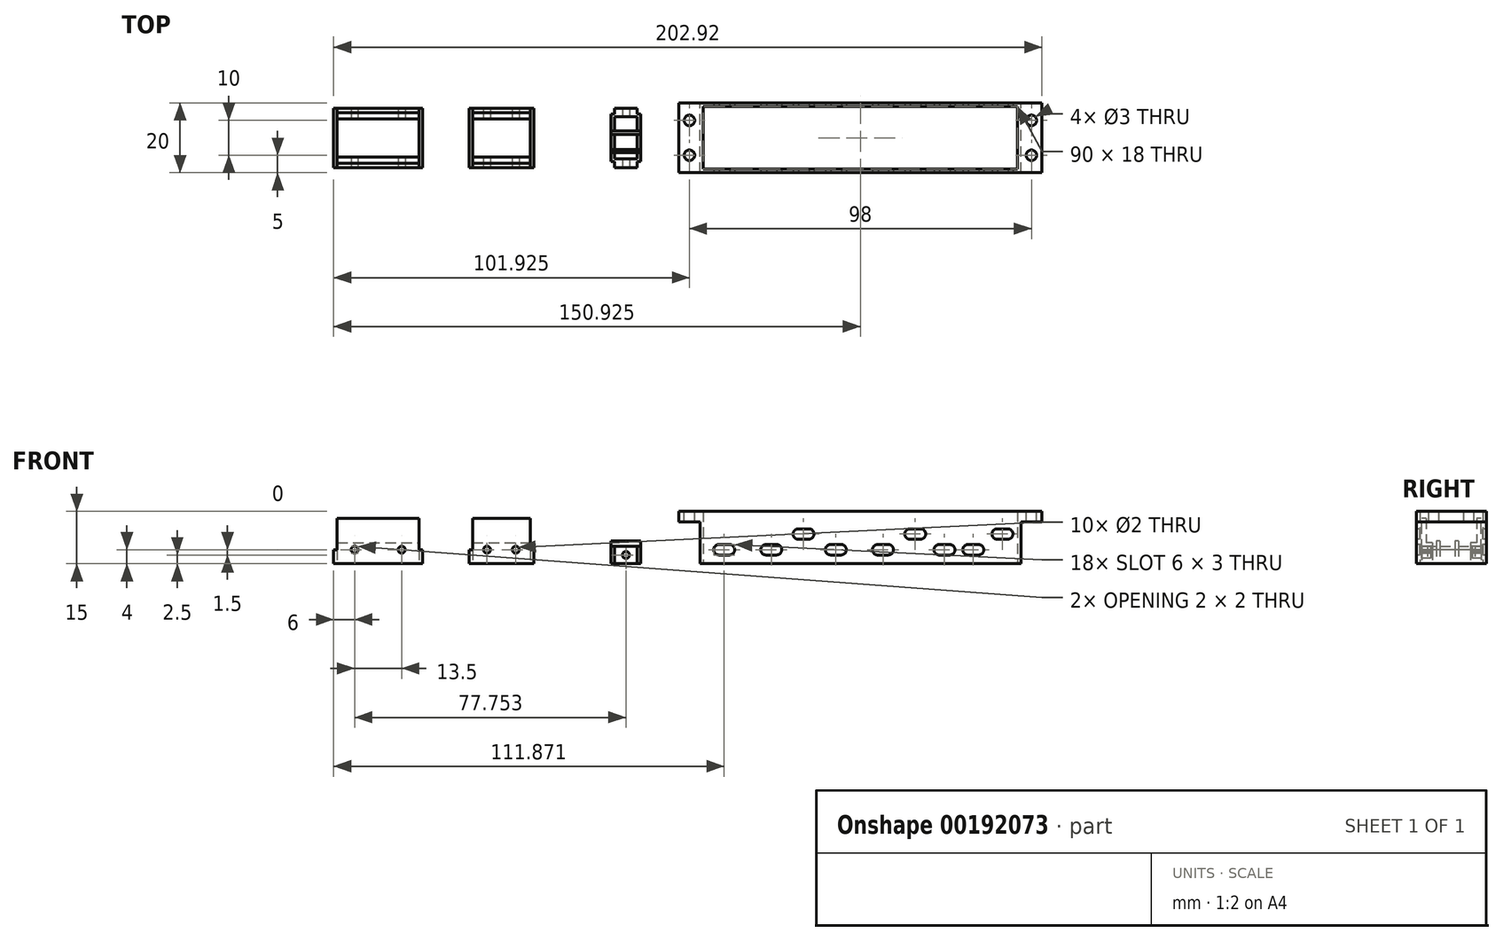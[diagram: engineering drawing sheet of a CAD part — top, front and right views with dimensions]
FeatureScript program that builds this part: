
annotation { "Feature Type Name" : "Feature", "Feature Type Description" : "" }
export const myFeature = defineFeature(function(context is Context, id is Id, definition is map)
    precondition{}
    {
        {
            var Q0;
            Q0=qCreatedBy(makeId("Top.planeOp"),FACE);
            var sketch = newSketch(context, id + "F0", { "sketchPlane" : qUnion([Q0])});
            skLineSegment(sketch, "E0.bottom", {"start": v(11.75, -7.25) * mm, "end": v(-11.75, -7.25) * mm});
            skLineSegment(sketch, "E0.top", {"start": v(11.75, 7.25) * mm, "end": v(-11.75, 7.25) * mm});
            skLineSegment(sketch, "E0.left", {"start": v(11.75, -7.25) * mm, "end": v(11.75, 7.25) * mm});
            skLineSegment(sketch, "E0.right", {"start": v(-11.75, -7.25) * mm, "end": v(-11.75, 7.25) * mm});
            skPoint(sketch, "E0.middle", {"position": v(0, 0) * mm});
            skLineSegment(sketch, "E1.bottom", {"start": v(12.75, -8.5) * mm, "end": v(-12.75, -8.5) * mm});
            skLineSegment(sketch, "E1.top", {"start": v(12.75, 8.5) * mm, "end": v(-12.75, 8.5) * mm});
            skLineSegment(sketch, "E1.left", {"start": v(12.75, -8.5) * mm, "end": v(12.75, 8.5) * mm});
            skLineSegment(sketch, "E1.right", {"start": v(-12.75, -8.5) * mm, "end": v(-12.75, 8.5) * mm});
            skLineSegment(sketch, "E2.bottom", {"start": v(26.05, -8.5) * mm, "end": v(44.55, -8.5) * mm});
            skLineSegment(sketch, "E2.top", {"start": v(26.05, 8.5) * mm, "end": v(44.55, 8.5) * mm});
            skLineSegment(sketch, "E2.left", {"start": v(26.05, -8.5) * mm, "end": v(26.05, 8.5) * mm});
            skLineSegment(sketch, "E2.right", {"start": v(44.55, -8.5) * mm, "end": v(44.55, 8.5) * mm});
            skPoint(sketch, "E2.middle", {"position": v(35.3, 0) * mm});
            skLineSegment(sketch, "E3.bottom", {"start": v(43.55, -7.25) * mm, "end": v(27.05, -7.25) * mm});
            skLineSegment(sketch, "E3.top", {"start": v(43.55, 7.25) * mm, "end": v(27.05, 7.25) * mm});
            skLineSegment(sketch, "E3.left", {"start": v(43.55, -7.25) * mm, "end": v(43.55, 7.25) * mm});
            skLineSegment(sketch, "E3.right", {"start": v(27.05, -7.25) * mm, "end": v(27.05, 7.25) * mm});
            skSolve(sketch);
        }
        {
            var Q0;
            Q0 = qSketchRegion(id + "F0", true);
            extrude(context, id + "F1", {"entities" : qUnion([Q0]), "depth" : 13 * mm});
        }
        {
            var Q0;
            Q0=qCreatedBy(makeId("Top.planeOp"),FACE);
            var sketch = newSketch(context, id + "F2", { "sketchPlane" : qUnion([Q0])});
            skLineSegment(sketch, "E4.bottom", {"start": v(-11.75, 7.25) * mm, "end": v(11.75, 7.25) * mm});
            skLineSegment(sketch, "E4.top", {"start": v(-11.75, 5.45) * mm, "end": v(11.75, 5.45) * mm});
            skLineSegment(sketch, "E4.left", {"start": v(-11.75, 7.25) * mm, "end": v(-11.75, 5.45) * mm});
            skLineSegment(sketch, "E4.right", {"start": v(11.75, 7.25) * mm, "end": v(11.75, 5.45) * mm});
            skLineSegment(sketch, "E5.bottom", {"start": v(-11.75, -5.45) * mm, "end": v(11.75, -5.45) * mm});
            skLineSegment(sketch, "E5.top", {"start": v(-11.75, -7.25) * mm, "end": v(11.75, -7.25) * mm});
            skLineSegment(sketch, "E5.left", {"start": v(-11.75, -5.45) * mm, "end": v(-11.75, -7.25) * mm});
            skLineSegment(sketch, "E5.right", {"start": v(11.75, -5.45) * mm, "end": v(11.75, -7.25) * mm});
            skLineSegment(sketch, "E6.bottom", {"start": v(27.05, 7.25) * mm, "end": v(43.55, 7.25) * mm});
            skLineSegment(sketch, "E6.top", {"start": v(27.05, 5.45) * mm, "end": v(43.55, 5.45) * mm});
            skLineSegment(sketch, "E6.left", {"start": v(27.05, 7.25) * mm, "end": v(27.05, 5.45) * mm});
            skLineSegment(sketch, "E6.right", {"start": v(43.55, 7.25) * mm, "end": v(43.55, 5.45) * mm});
            skLineSegment(sketch, "E7.bottom", {"start": v(27.05, -5.45) * mm, "end": v(43.55, -5.45) * mm});
            skLineSegment(sketch, "E7.top", {"start": v(27.05, -7.25) * mm, "end": v(43.55, -7.25) * mm});
            skLineSegment(sketch, "E7.left", {"start": v(27.05, -5.45) * mm, "end": v(27.05, -7.25) * mm});
            skLineSegment(sketch, "E7.right", {"start": v(43.55, -5.45) * mm, "end": v(43.55, -7.25) * mm});
            skSolve(sketch);
        }
        {
            var Q0;
            Q0 = qSketchRegion(id + "F2", true);
            extrude(context, id + "F3", {"entities" : qUnion([Q0]), "operationType" : NewBodyOperationType.ADD, "depth" : 6 * mm});
        }
        {
            var Q0;
            Q0=makeQuery(id+"F1.opExtrude","CAP_FACE",FACE,{"disambiguationData":[OSD([sQuery(id+"F0.wireOp",EDGE,"E0.bottom"),sQuery(id+"F0.wireOp",EDGE,"E0.top"),sQuery(id+"F0.wireOp",EDGE,"E0.left"),sQuery(id+"F0.wireOp",EDGE,"E0.right"),sQuery(id+"F0.wireOp",EDGE,"E1.bottom"),sQuery(id+"F0.wireOp",EDGE,"E1.top"),sQuery(id+"F0.wireOp",EDGE,"E1.left"),sQuery(id+"F0.wireOp",EDGE,"E1.right")])],"isStart":false});
            var sketch = newSketch(context, id + "F4", { "sketchPlane" : qUnion([Q0])});
            skLineSegment(sketch, "E8.bottom", {"start": v(-12.75, 8.5) * mm, "end": v(-11.75, 8.5) * mm});
            skLineSegment(sketch, "E8.top", {"start": v(-12.75, -8.5) * mm, "end": v(-11.75, -8.5) * mm});
            skLineSegment(sketch, "E8.left", {"start": v(-12.75, 8.5) * mm, "end": v(-12.75, -8.5) * mm});
            skLineSegment(sketch, "E8.right", {"start": v(-11.75, 8.5) * mm, "end": v(-11.75, -8.5) * mm});
            skLineSegment(sketch, "E9.bottom", {"start": v(12.75, 8.5) * mm, "end": v(11.75, 8.5) * mm});
            skLineSegment(sketch, "E9.top", {"start": v(12.75, -8.5) * mm, "end": v(11.75, -8.5) * mm});
            skLineSegment(sketch, "E9.left", {"start": v(12.75, 8.5) * mm, "end": v(12.75, -8.5) * mm});
            skLineSegment(sketch, "E9.right", {"start": v(11.75, 8.5) * mm, "end": v(11.75, -8.5) * mm});
            skLineSegment(sketch, "E10.bottom", {"start": v(26.05, 8.5) * mm, "end": v(27.05, 8.5) * mm});
            skLineSegment(sketch, "E10.top", {"start": v(26.05, -8.5) * mm, "end": v(27.05, -8.5) * mm});
            skLineSegment(sketch, "E10.left", {"start": v(26.05, 8.5) * mm, "end": v(26.05, -8.5) * mm});
            skLineSegment(sketch, "E10.right", {"start": v(27.05, 8.5) * mm, "end": v(27.05, -8.5) * mm});
            skLineSegment(sketch, "E11.bottom", {"start": v(43.55, 8.5) * mm, "end": v(44.55, 8.5) * mm});
            skLineSegment(sketch, "E11.top", {"start": v(43.55, -8.5) * mm, "end": v(44.55, -8.5) * mm});
            skLineSegment(sketch, "E11.left", {"start": v(43.55, 8.5) * mm, "end": v(43.55, -8.5) * mm});
            skLineSegment(sketch, "E11.right", {"start": v(44.55, 8.5) * mm, "end": v(44.55, -8.5) * mm});
            skSolve(sketch);
        }
        {
            var Q0;
            Q0 = qSketchRegion(id + "F4", true);
            extrude(context, id + "F5", {"entities" : qUnion([Q0]), "operationType" : NewBodyOperationType.REMOVE, "oppositeDirection" : true, "depth" : 9 * mm});
        }
        {
            var Q0;
            Q0=qCreatedBy(makeId("Top.planeOp"),FACE);
            var sketch = newSketch(context, id + "F6", { "sketchPlane" : qUnion([Q0])});
            skLineSegment(sketch, "E12.left", {"start": v(67.75, -8.5) * mm, "end": v(67.75, 8.5) * mm});
            skLineSegment(sketch, "E12.right", {"start": v(66.75, -6.8) * mm, "end": v(66.75, 6.8) * mm});
            skPoint(sketch, "E12.middle", {"position": v(67.25, 0) * mm});
            skLineSegment(sketch, "E13.left", {"start": v(74.25, -8.5) * mm, "end": v(74.25, 8.5) * mm});
            skLineSegment(sketch, "E13.right", {"start": v(75.25, -6.8) * mm, "end": v(75.25, 6.8) * mm});
            skPoint(sketch, "E13.middle", {"position": v(74.75, 0) * mm});
            skLineSegment(sketch, "E14.bottom", {"start": v(67.75, 8.5) * mm, "end": v(74.25, 8.5) * mm});
            skLineSegment(sketch, "E14.top", {"start": v(67.75, 6) * mm, "end": v(74.25, 6) * mm});
            skLineSegment(sketch, "E14.left", {"start": v(67.75, 8.5) * mm, "end": v(67.75, 6) * mm});
            skLineSegment(sketch, "E14.right", {"start": v(74.25, 8.5) * mm, "end": v(74.25, 6) * mm});
            skLineSegment(sketch, "E15.bottom", {"start": v(67.75, -8.5) * mm, "end": v(74.25, -8.5) * mm});
            skLineSegment(sketch, "E15.top", {"start": v(67.75, -6) * mm, "end": v(74.25, -6) * mm});
            skLineSegment(sketch, "E15.left", {"start": v(67.75, -8.5) * mm, "end": v(67.75, -6) * mm});
            skLineSegment(sketch, "E15.right", {"start": v(74.25, -8.5) * mm, "end": v(74.25, -6) * mm});
            skLineSegment(sketch, "E16", {"start": v(66.75, 6.8) * mm, "end": v(67.75, 6.8) * mm});
            skLineSegment(sketch, "E17", {"start": v(74.25, 6.8) * mm, "end": v(75.25, 6.8) * mm});
            skLineSegment(sketch, "E18", {"start": v(74.25, -6.8) * mm, "end": v(75.25, -6.8) * mm});
            skLineSegment(sketch, "E19", {"start": v(66.75, -6.8) * mm, "end": v(67.75, -6.8) * mm});
            skSolve(sketch);
        }
        {
            var Q0;
            Q0 = qSketchRegion(id + "F6", true);
            extrude(context, id + "F7", {"entities" : qUnion([Q0]), "depth" : 5 * mm});
        }
        {
            var Q0;
            Q0=makeQuery(id+"F1.opExtrude","SWEPT_FACE",FACE,{"disambiguationData":[OSD([sQuery(id+"F0.wireOp",EDGE,"E1.bottom")])]});
            var sketch = newSketch(context, id + "F8", { "sketchPlane" : qUnion([Q0])});
            skCircle(sketch, "E20", {"center": v(-6.75, 4) * mm, "radius": 1 * mm});
            skCircle(sketch, "E21", {"center": v(6.75, 4) * mm, "radius": 1 * mm});
            skCircle(sketch, "E22", {"center": v(31.18, 4) * mm, "radius": 1 * mm});
            skCircle(sketch, "E23", {"center": v(39.43, 4) * mm, "radius": 1 * mm});
            skCircle(sketch, "E24", {"center": v(71, 2.5) * mm, "radius": 1 * mm});
            skSolve(sketch);
        }
        {
            var Q0;
            Q0 = qSketchRegion(id + "F8", true);
            extrude(context, id + "F9", {"entities" : qUnion([Q0]), "operationType" : NewBodyOperationType.REMOVE, "oppositeDirection" : true, "depth" : 25 * mm});
        }
        {
            var Q0;
            Q0=qCreatedBy(makeId("Top.planeOp"),FACE);
            var sketch = newSketch(context, id + "F10", { "sketchPlane" : qUnion([Q0])});
            skLineSegment(sketch, "E25.bottom", {"start": v(66.75, 2) * mm, "end": v(75.25, 2) * mm});
            skLineSegment(sketch, "E25.top", {"start": v(66.75, 1) * mm, "end": v(75.25, 1) * mm});
            skLineSegment(sketch, "E25.left", {"start": v(66.75, 2) * mm, "end": v(66.75, 1) * mm});
            skLineSegment(sketch, "E25.right", {"start": v(75.25, 2) * mm, "end": v(75.25, 1) * mm});
            skLineSegment(sketch, "E26.bottom", {"start": v(66.75, -3.3) * mm, "end": v(75.25, -3.3) * mm});
            skLineSegment(sketch, "E26.top", {"start": v(66.75, -4.3) * mm, "end": v(75.25, -4.3) * mm});
            skLineSegment(sketch, "E26.left", {"start": v(66.75, -3.3) * mm, "end": v(66.75, -4.3) * mm});
            skLineSegment(sketch, "E26.right", {"start": v(75.25, -3.3) * mm, "end": v(75.25, -4.3) * mm});
            skSolve(sketch);
        }
        {
            var Q0;
            Q0 = qSketchRegion(id + "F10", true);
            extrude(context, id + "F11", {"entities" : qUnion([Q0]), "operationType" : NewBodyOperationType.ADD, "depth" : 6.5 * mm});
        }
        {
            var Q0;
            Q0=qCreatedBy(makeId("Top.planeOp"),FACE);
            var sketch = newSketch(context, id + "F12", { "sketchPlane" : qUnion([Q0])});
            skLineSegment(sketch, "E27.bottom", {"start": v(183.17, -9) * mm, "end": v(93.17, -9) * mm});
            skLineSegment(sketch, "E27.top", {"start": v(183.17, 9) * mm, "end": v(93.17, 9) * mm});
            skLineSegment(sketch, "E27.left", {"start": v(183.17, -9) * mm, "end": v(183.17, 9) * mm});
            skLineSegment(sketch, "E27.right", {"start": v(93.17, -9) * mm, "end": v(93.17, 9) * mm});
            skPoint(sketch, "E27.middle", {"position": v(138.17, 0) * mm});
            skLineSegment(sketch, "E28.bottom", {"start": v(184.17, -10) * mm, "end": v(92.17, -10) * mm});
            skLineSegment(sketch, "E28.top", {"start": v(184.17, 10) * mm, "end": v(92.17, 10) * mm});
            skLineSegment(sketch, "E28.left", {"start": v(184.17, -10) * mm, "end": v(184.17, 10) * mm});
            skLineSegment(sketch, "E28.right", {"start": v(92.17, -10) * mm, "end": v(92.17, 10) * mm});
            skSolve(sketch);
        }
        {
            var Q0;
            Q0 = qSketchRegion(id + "F12", true);
            extrude(context, id + "F13", {"entities" : qUnion([Q0]), "depth" : 15 * mm});
        }
        {
            var Q0;
            Q0=makeQuery(id+"F13.opExtrude","CAP_FACE",FACE,{"disambiguationData":[OSD([sQuery(id+"F12.wireOp",EDGE,"E27.bottom"),sQuery(id+"F12.wireOp",EDGE,"E27.top"),sQuery(id+"F12.wireOp",EDGE,"E27.left"),sQuery(id+"F12.wireOp",EDGE,"E27.right"),sQuery(id+"F12.wireOp",EDGE,"E28.bottom"),sQuery(id+"F12.wireOp",EDGE,"E28.top"),sQuery(id+"F12.wireOp",EDGE,"E28.left"),sQuery(id+"F12.wireOp",EDGE,"E28.right")])],"isStart":false});
            var sketch = newSketch(context, id + "F14", { "sketchPlane" : qUnion([Q0])});
            skLineSegment(sketch, "E29.bottom", {"start": v(92.17, 10) * mm, "end": v(86.17, 10) * mm});
            skLineSegment(sketch, "E29.top", {"start": v(92.17, -10) * mm, "end": v(86.17, -10) * mm});
            skLineSegment(sketch, "E29.left", {"start": v(92.17, 10) * mm, "end": v(92.17, -10) * mm});
            skLineSegment(sketch, "E29.right", {"start": v(86.17, 10) * mm, "end": v(86.17, -10) * mm});
            skLineSegment(sketch, "E30.bottom", {"start": v(184.17, 10) * mm, "end": v(190.17, 10) * mm});
            skLineSegment(sketch, "E30.top", {"start": v(184.17, -10) * mm, "end": v(190.17, -10) * mm});
            skLineSegment(sketch, "E30.left", {"start": v(184.17, 10) * mm, "end": v(184.17, -10) * mm});
            skLineSegment(sketch, "E30.right", {"start": v(190.17, 10) * mm, "end": v(190.17, -10) * mm});
            skCircle(sketch, "E31", {"center": v(89.17, 5) * mm, "radius": 1.5 * mm});
            skCircle(sketch, "E32", {"center": v(89.17, -5) * mm, "radius": 1.5 * mm});
            skCircle(sketch, "E33", {"center": v(187.17, 5) * mm, "radius": 1.5 * mm});
            skCircle(sketch, "E34", {"center": v(187.17, -5) * mm, "radius": 1.5 * mm});
            skSolve(sketch);
        }
        {
            var Q0;
            Q0 = qSketchRegion(id + "F14", true);
            extrude(context, id + "F15", {"entities" : qUnion([Q0]), "operationType" : NewBodyOperationType.ADD, "oppositeDirection" : true, "depth" : 3 * mm});
        }
        {
            var Q0;
            Q0=makeQuery(id+"F15.boolean.opBoolean","MERGE",FACE,{"derivedFrom":[makeQuery(id+"F13.opExtrude","SWEPT_FACE",FACE,{"disambiguationData":[OSD([sQuery(id+"F12.wireOp",EDGE,"E28.bottom")])]}),makeQuery(id+"F15.opExtrude","SWEPT_FACE",FACE,{"disambiguationData":[OSD([sQuery(id+"F14.wireOp",EDGE,"E29.top")])]}),makeQuery(id+"F15.opExtrude","SWEPT_FACE",FACE,{"disambiguationData":[OSD([sQuery(id+"F14.wireOp",EDGE,"E30.top")])]})]});
            var sketch = newSketch(context, id + "F16", { "sketchPlane" : qUnion([Q0])});
            skLineSegment(sketch, "E35.bottom", {"start": v(100.73, 2.5) * mm, "end": v(97.73, 2.5) * mm});
            skLineSegment(sketch, "E35.top", {"start": v(100.62, 5.5) * mm, "end": v(97.62, 5.5) * mm});
            skPoint(sketch, "E35.middle", {"position": v(99.17, 4) * mm});
            skArc(sketch, "E36", {"start": v(97.62, 5.5) * mm, "mid": v(96.12, 3.94) * mm, "end": v(97.73, 2.5) * mm});
            skArc(sketch, "E37", {"start": v(100.62, 5.5) * mm, "mid": v(102.12, 4.05) * mm, "end": v(100.73, 2.5) * mm});
            skLineSegment(sketch, "E38.bottom", {"start": v(114.23, 2.5) * mm, "end": v(111.23, 2.5) * mm});
            skLineSegment(sketch, "E38.top", {"start": v(114.12, 5.5) * mm, "end": v(111.12, 5.5) * mm});
            skPoint(sketch, "E38.middle", {"position": v(112.67, 4) * mm});
            skArc(sketch, "E39", {"start": v(111.12, 5.5) * mm, "mid": v(109.62, 3.94) * mm, "end": v(111.23, 2.5) * mm});
            skArc(sketch, "E40", {"start": v(114.12, 5.5) * mm, "mid": v(115.62, 4.05) * mm, "end": v(114.23, 2.5) * mm});
            skLineSegment(sketch, "E41.bottom", {"start": v(132.73, 2.5) * mm, "end": v(129.73, 2.5) * mm});
            skLineSegment(sketch, "E41.top", {"start": v(132.62, 5.5) * mm, "end": v(129.62, 5.5) * mm});
            skPoint(sketch, "E41.middle", {"position": v(131.17, 4) * mm});
            skArc(sketch, "E42", {"start": v(129.62, 5.5) * mm, "mid": v(128.12, 3.94) * mm, "end": v(129.73, 2.5) * mm});
            skArc(sketch, "E43", {"start": v(132.62, 5.5) * mm, "mid": v(134.12, 4.05) * mm, "end": v(132.73, 2.5) * mm});
            skLineSegment(sketch, "E44.bottom", {"start": v(146.23, 2.5) * mm, "end": v(143.23, 2.5) * mm});
            skLineSegment(sketch, "E44.top", {"start": v(146.12, 5.5) * mm, "end": v(143.12, 5.5) * mm});
            skPoint(sketch, "E44.middle", {"position": v(144.67, 4) * mm});
            skArc(sketch, "E45", {"start": v(143.12, 5.5) * mm, "mid": v(141.62, 3.94) * mm, "end": v(143.23, 2.5) * mm});
            skArc(sketch, "E46", {"start": v(146.12, 5.5) * mm, "mid": v(147.62, 4.05) * mm, "end": v(146.23, 2.5) * mm});
            skLineSegment(sketch, "E47.bottom", {"start": v(163.85, 2.5) * mm, "end": v(160.85, 2.5) * mm});
            skLineSegment(sketch, "E47.top", {"start": v(163.75, 5.5) * mm, "end": v(160.75, 5.5) * mm});
            skPoint(sketch, "E47.middle", {"position": v(162.3, 4) * mm});
            skArc(sketch, "E48", {"start": v(160.75, 5.5) * mm, "mid": v(159.24, 3.94) * mm, "end": v(160.85, 2.5) * mm});
            skArc(sketch, "E49", {"start": v(163.75, 5.5) * mm, "mid": v(165.25, 4.04) * mm, "end": v(163.85, 2.5) * mm});
            skLineSegment(sketch, "E50.bottom", {"start": v(172.1, 2.5) * mm, "end": v(169.1, 2.5) * mm});
            skLineSegment(sketch, "E50.top", {"start": v(172, 5.5) * mm, "end": v(169, 5.5) * mm});
            skPoint(sketch, "E50.middle", {"position": v(170.55, 4) * mm});
            skArc(sketch, "E51", {"start": v(169, 5.5) * mm, "mid": v(167.5, 3.93) * mm, "end": v(169.1, 2.5) * mm});
            skArc(sketch, "E52", {"start": v(172, 5.5) * mm, "mid": v(173.5, 4.04) * mm, "end": v(172.1, 2.5) * mm});
            skLineSegment(sketch, "E53.bottom", {"start": v(123.48, 7) * mm, "end": v(120.48, 7) * mm});
            skLineSegment(sketch, "E53.top", {"start": v(123.37, 10) * mm, "end": v(120.37, 10) * mm});
            skPoint(sketch, "E53.middle", {"position": v(121.92, 8.5) * mm});
            skArc(sketch, "E54", {"start": v(120.37, 10) * mm, "mid": v(118.87, 8.44) * mm, "end": v(120.48, 7) * mm});
            skArc(sketch, "E55", {"start": v(123.37, 10) * mm, "mid": v(124.87, 8.55) * mm, "end": v(123.48, 7) * mm});
            skLineSegment(sketch, "E56.bottom", {"start": v(155.48, 7) * mm, "end": v(152.48, 7) * mm});
            skLineSegment(sketch, "E56.top", {"start": v(155.37, 10) * mm, "end": v(152.37, 10) * mm});
            skPoint(sketch, "E56.middle", {"position": v(153.92, 8.5) * mm});
            skArc(sketch, "E57", {"start": v(152.37, 10) * mm, "mid": v(150.87, 8.44) * mm, "end": v(152.48, 7) * mm});
            skArc(sketch, "E58", {"start": v(155.37, 10) * mm, "mid": v(156.87, 8.55) * mm, "end": v(155.48, 7) * mm});
            skLineSegment(sketch, "E59.bottom", {"start": v(180.48, 7) * mm, "end": v(177.48, 7) * mm});
            skLineSegment(sketch, "E59.top", {"start": v(180.37, 10) * mm, "end": v(177.37, 10) * mm});
            skPoint(sketch, "E59.middle", {"position": v(178.92, 8.5) * mm});
            skArc(sketch, "E60", {"start": v(177.37, 10) * mm, "mid": v(175.87, 8.44) * mm, "end": v(177.48, 7) * mm});
            skArc(sketch, "E61", {"start": v(180.37, 10) * mm, "mid": v(181.87, 8.55) * mm, "end": v(180.48, 7) * mm});
            skLineSegment(sketch, "E62", {"start": v(93.17, 23.62) * mm, "end": v(93.17, -20.74) * mm, "construction": true});
            skLineSegment(sketch, "E63", {"start": v(118.67, 24.54) * mm, "end": v(118.67, -21.54) * mm, "construction": true});
            skLineSegment(sketch, "E64", {"start": v(125.17, 27.3) * mm, "end": v(125.17, -21.1) * mm, "construction": true});
            skLineSegment(sketch, "E65", {"start": v(150.67, 37.38) * mm, "end": v(150.67, -22.48) * mm, "construction": true});
            skLineSegment(sketch, "E66", {"start": v(157.17, 36.57) * mm, "end": v(157.17, -21.16) * mm, "construction": true});
            skLineSegment(sketch, "E67", {"start": v(175.67, 37.2) * mm, "end": v(175.67, -19.6) * mm, "construction": true});
            skLineSegment(sketch, "E68", {"start": v(182.17, -11.38) * mm, "end": v(182.17, 35.18) * mm, "construction": true});
            skSolve(sketch);
        }
        {
            var Q0;
            Q0 = qSketchRegion(id + "F16", true);
            extrude(context, id + "F17", {"entities" : qUnion([Q0]), "operationType" : NewBodyOperationType.REMOVE, "oppositeDirection" : true, "depth" : 25 * mm});
        }
    });
